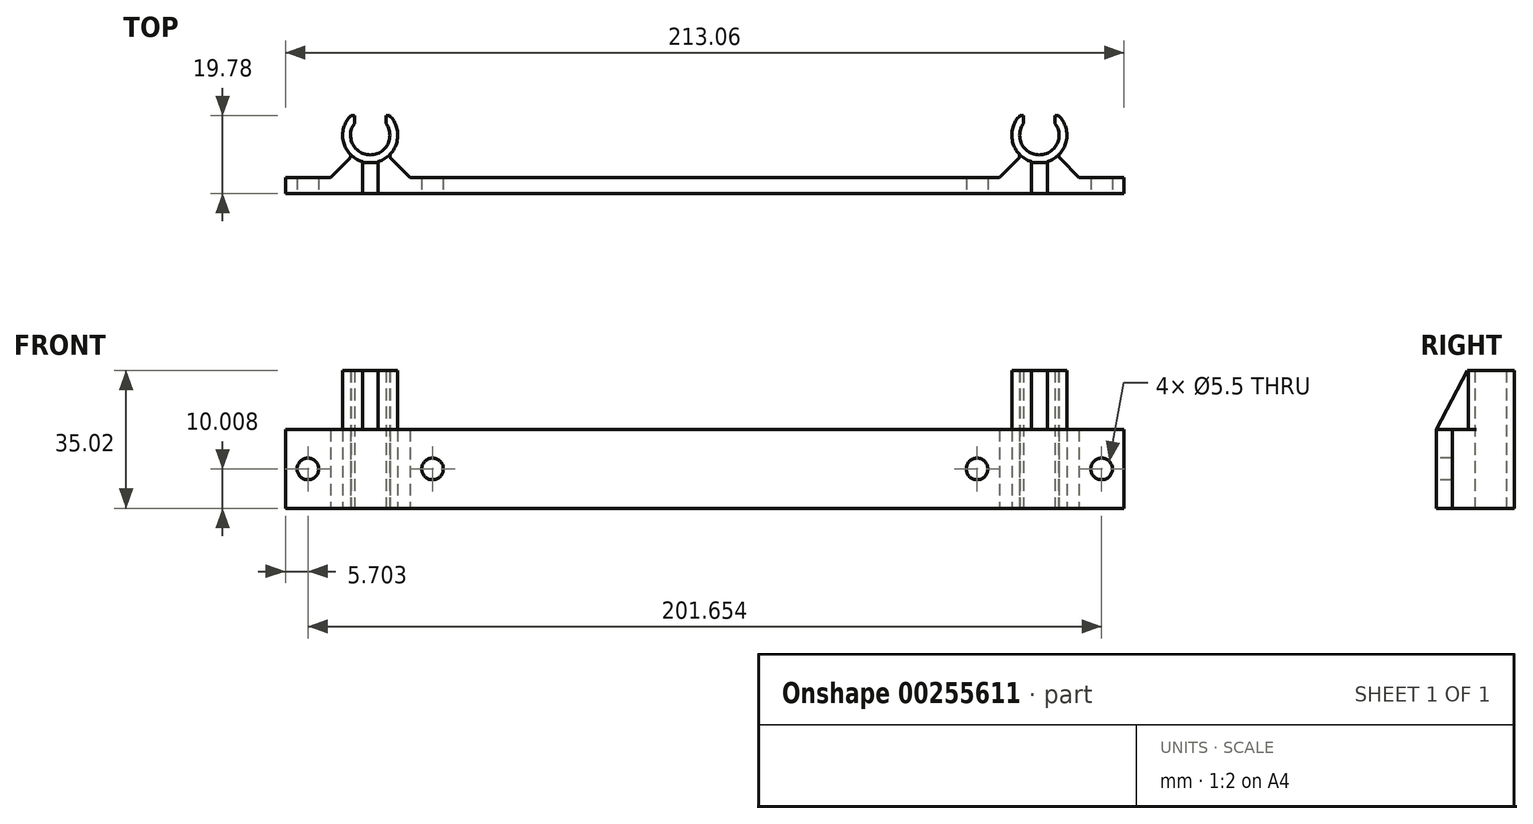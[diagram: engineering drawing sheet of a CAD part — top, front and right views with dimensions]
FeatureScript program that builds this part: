
annotation { "Feature Type Name" : "Feature", "Feature Type Description" : "" }
export const myFeature = defineFeature(function(context is Context, id is Id, definition is map)
    precondition{}
    {
        {
            var Q0;
            Q0=qCreatedBy(makeId("Top.planeOp"),FACE);
            var sketch = newSketch(context, id + "F0", { "sketchPlane" : qUnion([Q0])});
            skArc(sketch, "E0", {"start": v(-89, 3) * mm, "mid": v(-85, -5) * mm, "end": v(-81, 3) * mm});
            skArc(sketch, "E1.MirrorC", {"start": v(89, 3) * mm, "mid": v(85, -5) * mm, "end": v(81, 3) * mm});
            skLineSegment(sketch, "E2", {"start": v(-106.53, -14.78) * mm, "end": v(106.53, -14.78) * mm});
            skLineSegment(sketch, "E3", {"start": v(106.53, -14.78) * mm, "end": v(106.53, -10.78) * mm});
            skLineSegment(sketch, "E4", {"start": v(106.53, -10.78) * mm, "end": v(95.08, -10.78) * mm});
            skLineSegment(sketch, "E5", {"start": v(-106.53, -10.78) * mm, "end": v(-106.53, -14.78) * mm});
            skArc(sketch, "E6", {"start": v(-89.9, 5) * mm, "mid": v(-92, 0.25) * mm, "end": v(-90.25, -4.63) * mm});
            skLineSegment(sketch, "E7", {"start": v(-85, 0) * mm, "end": v(-85, 11.64) * mm, "construction": true});
            skLineSegment(sketch, "E8", {"start": v(-89.9, 5) * mm, "end": v(-89, 5) * mm});
            skLineSegment(sketch, "E9", {"start": v(-89, 5) * mm, "end": v(-89, 3) * mm});
            skLineSegment(sketch, "E10", {"start": v(-81, 5) * mm, "end": v(-81, 3) * mm});
            skLineSegment(sketch, "E11.trimOffspring", {"start": v(-81, 5) * mm, "end": v(-80.1, 5) * mm});
            skArc(sketch, "E12.trimOffspring", {"start": v(-79.75, -4.63) * mm, "mid": v(-78, 0.25) * mm, "end": v(-80.1, 5) * mm});
            skArc(sketch, "E13.MirrorCS", {"start": v(89.9, 5) * mm, "mid": v(92, 0.25) * mm, "end": v(90.25, -4.63) * mm});
            skArc(sketch, "E14.MirrorCS", {"start": v(79.75, -4.63) * mm, "mid": v(78, 0.25) * mm, "end": v(80.1, 5) * mm});
            skLineSegment(sketch, "E15.MirrorCS", {"start": v(89.9, 5) * mm, "end": v(89, 5) * mm});
            skLineSegment(sketch, "E16.MirrorCS", {"start": v(89, 5) * mm, "end": v(89, 3) * mm});
            skLineSegment(sketch, "E17.MirrorCS", {"start": v(81, 5) * mm, "end": v(80.1, 5) * mm});
            skLineSegment(sketch, "E18.MirrorCS", {"start": v(81, 5) * mm, "end": v(81, 3) * mm});
            skLineSegment(sketch, "E19.trimOffspring", {"start": v(74.92, -10.78) * mm, "end": v(-74.92, -10.78) * mm});
            skLineSegment(sketch, "E20.trimOffspring", {"start": v(-95.08, -10.78) * mm, "end": v(-106.53, -10.78) * mm});
            skLineSegment(sketch, "E21", {"start": v(-95.08, -10.78) * mm, "end": v(-90.3, -6) * mm});
            skArc(sketch, "E22", {"start": v(-90.3, -6) * mm, "mid": v(-90, -5.32) * mm, "end": v(-90.25, -4.63) * mm});
            skArc(sketch, "E23.MirrorCS", {"start": v(-79.7, -6) * mm, "mid": v(-80, -5.32) * mm, "end": v(-79.75, -4.63) * mm});
            skLineSegment(sketch, "E24.MirrorCS", {"start": v(-74.92, -10.78) * mm, "end": v(-79.7, -6) * mm});
            skLineSegment(sketch, "E25.MirrorCS", {"start": v(95.08, -10.78) * mm, "end": v(90.3, -6) * mm});
            skLineSegment(sketch, "E26.MirrorCS", {"start": v(74.92, -10.78) * mm, "end": v(79.7, -6) * mm});
            skArc(sketch, "E27.MirrorCS", {"start": v(79.7, -6) * mm, "mid": v(80, -5.32) * mm, "end": v(79.75, -4.63) * mm});
            skArc(sketch, "E28.MirrorCS", {"start": v(90.3, -6) * mm, "mid": v(90, -5.32) * mm, "end": v(90.25, -4.63) * mm});
            skSolve(sketch);
        }
        {
            var Q0;
            Q0=makeQuery(id+"F0.imprint","IMPRINT",FACE,{"disambiguationData":[TD([[makeQuery(id+"F0.imprint","IMPRINT",EDGE,{"derivedFrom":sQuery(id+"F0.wireOp",EDGE,"E0")}),-1.0]])]});
            extrude(context, id + "F1", {"entities" : qUnion([Q0]), "depth" : 20.02 * mm});
        }
        {
            var Q0;
            Q0=makeQuery(id+"F1.opExtrude","CAP_FACE",FACE,{"disambiguationData":[OSD([sQuery(id+"F0.wireOp",EDGE,"E0"),sQuery(id+"F0.wireOp",EDGE,"E1.MirrorC"),sQuery(id+"F0.wireOp",EDGE,"E2"),sQuery(id+"F0.wireOp",EDGE,"E3"),sQuery(id+"F0.wireOp",EDGE,"E4"),sQuery(id+"F0.wireOp",EDGE,"E5"),sQuery(id+"F0.wireOp",EDGE,"E6"),sQuery(id+"F0.wireOp",EDGE,"XfPZOTKn-CBuq-HJ1q-0B4a-VGRrlxXO2UET"),sQuery(id+"F0.wireOp",EDGE,"6yOg2JvU-q7Ur-jJvM-rkNV-jBIDe4iiKgh4"),sQuery(id+"F0.wireOp",EDGE,"E8"),sQuery(id+"F0.wireOp",EDGE,"E9"),sQuery(id+"F0.wireOp",EDGE,"E10"),sQuery(id+"F0.wireOp",EDGE,"E11.trimOffspring"),sQuery(id+"F0.wireOp",EDGE,"E12.trimOffspring"),sQuery(id+"F0.wireOp",EDGE,"E13.MirrorCS"),sQuery(id+"F0.wireOp",EDGE,"E14.MirrorCS"),sQuery(id+"F0.wireOp",EDGE,"919f7e70-29dc-403c-beaf-e72550aa5eaa0.MirrorCS"),sQuery(id+"F0.wireOp",EDGE,"73e56539-6512-40c9-8321-30adb04f3fef0.MirrorCS"),sQuery(id+"F0.wireOp",EDGE,"E15.MirrorCS"),sQuery(id+"F0.wireOp",EDGE,"E16.MirrorCS"),sQuery(id+"F0.wireOp",EDGE,"E17.MirrorCS"),sQuery(id+"F0.wireOp",EDGE,"E18.MirrorCS"),sQuery(id+"F0.wireOp",EDGE,"E19.trimOffspring"),sQuery(id+"F0.wireOp",EDGE,"E20.trimOffspring")])],"isStart":false});
            var sketch = newSketch(context, id + "F2", { "sketchPlane" : qUnion([Q0])});
            skArc(sketch, "E29", {"start": v(-89.9, 5) * mm, "mid": v(-85, -7) * mm, "end": v(-80.1, 5) * mm});
            skLineSegment(sketch, "E30.0", {"start": v(-89.9, 5) * mm, "end": v(-89, 5) * mm});
            skLineSegment(sketch, "E31.0", {"start": v(-89, 5) * mm, "end": v(-89, 3) * mm});
            skArc(sketch, "E32.0", {"start": v(-89, 3) * mm, "mid": v(-85, -5) * mm, "end": v(-81, 3) * mm});
            skLineSegment(sketch, "E33.0", {"start": v(-81, 5) * mm, "end": v(-81, 3) * mm});
            skLineSegment(sketch, "E34.0", {"start": v(-81, 5) * mm, "end": v(-80.1, 5) * mm});
            skLineSegment(sketch, "E35.MirrorCS", {"start": v(81, 5) * mm, "end": v(80.1, 5) * mm});
            skLineSegment(sketch, "E36.MirrorCS", {"start": v(81, 5) * mm, "end": v(81, 3) * mm});
            skLineSegment(sketch, "E37.MirrorCS", {"start": v(89, 5) * mm, "end": v(89, 3) * mm});
            skLineSegment(sketch, "E38.MirrorCS", {"start": v(89.9, 5) * mm, "end": v(89, 5) * mm});
            skArc(sketch, "E39.MirrorCS", {"start": v(89.9, 5) * mm, "mid": v(85, -7) * mm, "end": v(80.1, 5) * mm});
            skArc(sketch, "E40.MirrorCS", {"start": v(89, 3) * mm, "mid": v(85, -5) * mm, "end": v(81, 3) * mm});
            skSolve(sketch);
        }
        {
            var Q0;
            {var subQ0=sQuery(id+"F2.wireOp",EDGE,"E30.0");Q0=makeQuery(id+"F2.imprint","IMPRINT",FACE,{"disambiguationData":[TD([[makeQuery(id+"F2.imprint","IMPRINT",EDGE,{"derivedFrom":subQ0}),-1.0]])]});}
            var Q1;
            {var subQ1=sQuery(id+"F2.wireOp",EDGE,"E35.MirrorCS");Q1=makeQuery(id+"F2.imprint","IMPRINT",FACE,{"disambiguationData":[TD([[makeQuery(id+"F2.imprint","IMPRINT",EDGE,{"derivedFrom":subQ1}),1.0]])]});}
            extrude(context, id + "F3", {"entities" : qUnion([Q0, Q1]), "operationType" : NewBodyOperationType.ADD, "depth" : 15 * mm});
        }
        {
            var Q0;
            Q0=makeQuery(id+"F1.opExtrude","SWEPT_FACE",FACE,{"disambiguationData":[OSD([sQuery(id+"F0.wireOp",EDGE,"E2")])]});
            var sketch = newSketch(context, id + "F4", { "sketchPlane" : qUnion([Q0])});
            skCircle(sketch, "E41", {"center": v(-100.83, 10) * mm, "radius": 2.75 * mm});
            skPoint(sketch, "E41.centerSnap0", {"position": v(-106.53, 10) * mm});
            skCircle(sketch, "E42", {"center": v(-69.17, 10) * mm, "radius": 2.75 * mm});
            skCircle(sketch, "E43", {"center": v(-100.83, 10) * mm, "radius": 5.75 * mm, "construction": true});
            skCircle(sketch, "E44", {"center": v(-69.17, 10) * mm, "radius": 5.75 * mm, "construction": true});
            skCircle(sketch, "E45.MirrorC", {"center": v(69.17, 10) * mm, "radius": 2.75 * mm});
            skCircle(sketch, "E46.MirrorC", {"center": v(100.83, 10) * mm, "radius": 2.75 * mm});
            skSolve(sketch);
        }
        {
            var Q0;
            Q0 = qSketchRegion(id + "F4", true);
            extrude(context, id + "F5", {"entities" : qUnion([Q0]), "operationType" : NewBodyOperationType.REMOVE, "endBound" : BoundingType.THROUGH_ALL, "oppositeDirection" : true, "depth" : 25 * mm});
        }
        {
            var Q0;
            Q0=qCreatedBy(makeId("Right.planeOp"),FACE);
            cPlane(context, id + "F6", {"entities" : qUnion([Q0]), "cplaneType" : CPlaneType.OFFSET, "offset" : (170 / 2 + 2) * mm, "oppositeDirection" : true, "width" : 150 * mm, "height" : 150 * mm});
        }
        {
            var Q0;
            Q0=qCreatedBy(id+"F6.planeOp",FACE);
            var sketch = newSketch(context, id + "F7", { "sketchPlane" : qUnion([Q0])});
            skLineSegment(sketch, "E47", {"start": v(-14.78, 20.02) * mm, "end": v(-7, 35.02) * mm});
            skLineSegment(sketch, "E48", {"start": v(-14.78, 20.02) * mm, "end": v(-6, 20.02) * mm});
            skLineSegment(sketch, "E49", {"start": v(-6, 20.02) * mm, "end": v(-6, 35.02) * mm});
            skLineSegment(sketch, "E50", {"start": v(-7, 35.02) * mm, "end": v(-6, 35.02) * mm});
            skLineSegment(sketch, "E51", {"start": v(-7, 19.05) * mm, "end": v(-7, 35.02) * mm, "construction": true});
            skSolve(sketch);
        }
        {
            var Q0;
            Q0=makeQuery(id+"F7.imprint","IMPRINT",FACE,{"disambiguationData":[TD([[makeQuery(id+"F7.imprint","IMPRINT",EDGE,{"derivedFrom":sQuery(id+"F7.wireOp",EDGE,"E47")}),-1.0]])]});
            extrude(context, id + "F8", {"entities" : qUnion([Q0]), "depth" : 4 * mm});
        }
        {
            var Q0;
            Q0=makeQuery(id+"F8.opExtrude","SWEPT_BODY",BODY,{"disambiguationData":[OSD([sQuery(id+"F7.wireOp",EDGE,"E47"),sQuery(id+"F7.wireOp",EDGE,"E48"),sQuery(id+"F7.wireOp",EDGE,"E49"),sQuery(id+"F7.wireOp",EDGE,"E50")])]});
            var Q1;
            Q1=qCreatedBy(makeId("Right.planeOp"),FACE);
            mirror(context, id + "F9", {"operationType" : NewBodyOperationType.ADD, "entities" : qUnion([Q0]), "mirrorPlane" : qUnion([Q1])});
        }
    });
